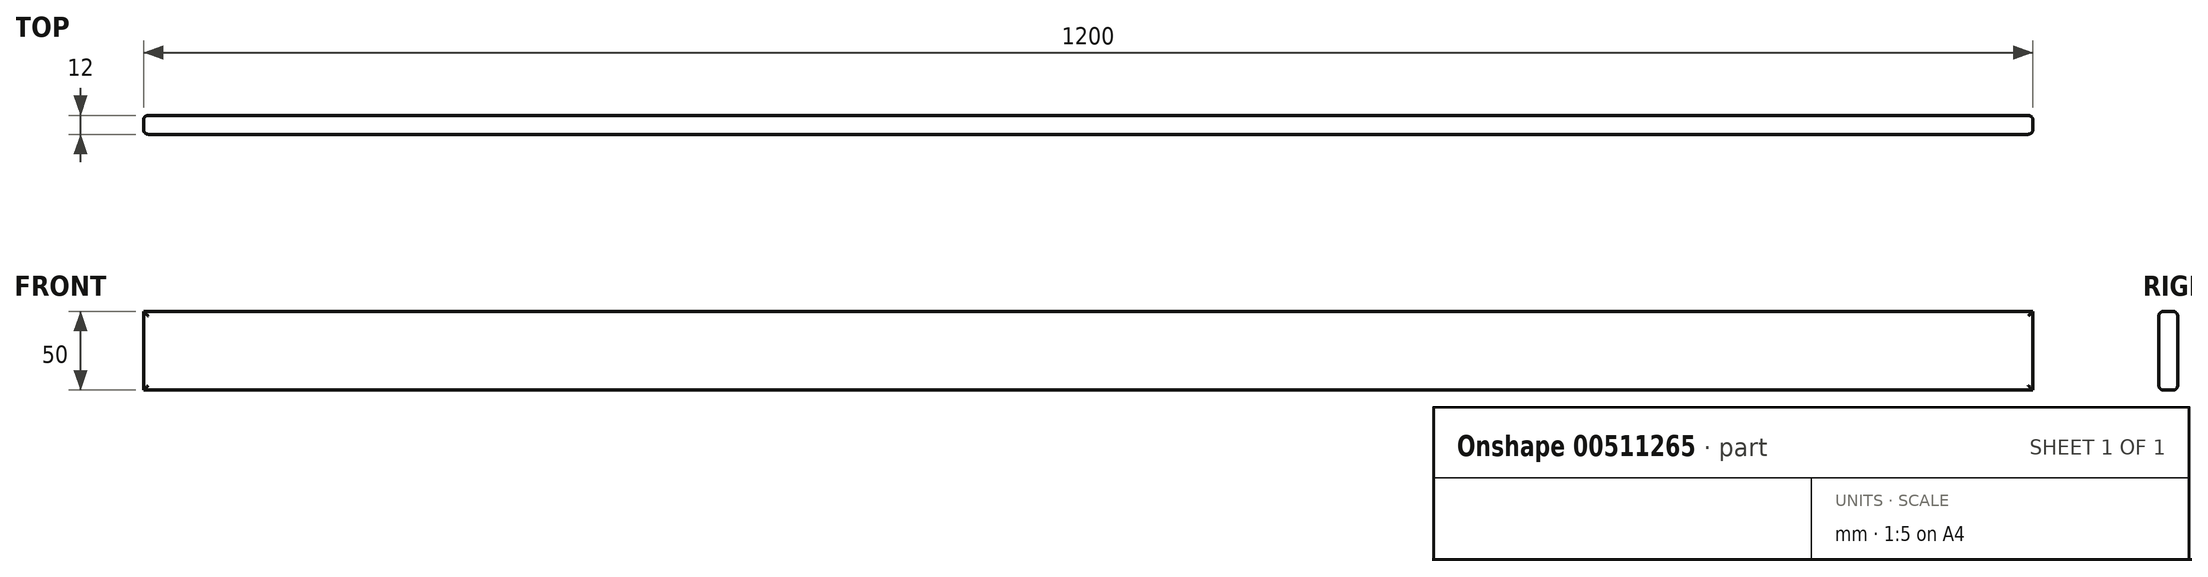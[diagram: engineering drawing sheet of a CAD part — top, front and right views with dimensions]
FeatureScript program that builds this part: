
annotation { "Feature Type Name" : "Feature", "Feature Type Description" : "" }
export const myFeature = defineFeature(function(context is Context, id is Id, definition is map)
    precondition{}
    {
        {
            var Q0;
            Q0=qCreatedBy(makeId("Front.planeOp"),FACE);
            var sketch = newSketch(context, id + "F0", { "sketchPlane" : qUnion([Q0])});
            skLineSegment(sketch, "E0.bottom", {"start": v(-600.37, 30.64) * mm, "end": v(599.63, 30.64) * mm});
            skLineSegment(sketch, "E0.top", {"start": v(-600.37, -19.36) * mm, "end": v(599.63, -19.36) * mm});
            skLineSegment(sketch, "E0.left", {"start": v(-600.37, 30.64) * mm, "end": v(-600.37, -19.36) * mm});
            skLineSegment(sketch, "E0.right", {"start": v(599.63, 30.64) * mm, "end": v(599.63, -19.36) * mm});
            skSolve(sketch);
        }
        {
            var Q0;
            Q0=makeQuery(id+"F0.imprint","IMPRINT",FACE,{"disambiguationData":[TD([[makeQuery(id+"F0.imprint","IMPRINT",EDGE,{"derivedFrom":sQuery(id+"F0.wireOp",EDGE,"E0.bottom")}),-1.0]])]});
            extrude(context, id + "F1", {"entities" : qUnion([Q0]), "depth" : 12 * mm});
        }
        {
            var Q0;
            Q0=makeQuery(id+"F1.opExtrude","CAP_FACE",FACE,{"disambiguationData":[OSD([sQuery(id+"F0.wireOp",EDGE,"E0.bottom"),sQuery(id+"F0.wireOp",EDGE,"E0.top"),sQuery(id+"F0.wireOp",EDGE,"E0.left"),sQuery(id+"F0.wireOp",EDGE,"E0.right")])],"isStart":true});
            var Q1;
            Q1=makeQuery(id+"F1.opExtrude","CAP_FACE",FACE,{"disambiguationData":[OSD([sQuery(id+"F0.wireOp",EDGE,"E0.bottom"),sQuery(id+"F0.wireOp",EDGE,"E0.top"),sQuery(id+"F0.wireOp",EDGE,"E0.left"),sQuery(id+"F0.wireOp",EDGE,"E0.right")])],"isStart":false});
            fillet(context, id + "F2", {"entities" : qUnion([Q0, Q1]), "radius" : 3 * mm, "tangentPropagation" : true, "allowEdgeOverflow" : false});
        }
    });
